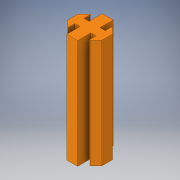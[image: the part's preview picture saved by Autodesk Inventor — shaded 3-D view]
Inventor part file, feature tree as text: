
AUTODESK INVENTOR PART (.ipt)
format: ipt  version: 2019 (Build 230136000, 136)  size: 141,824 bytes
history: native  units: in
note: dims shown in document units (in); Inventor stores cm internally (conversion verified against a paired STEP export)
features: extrude x1, fillet x1, sketch x1
ambient origin geometry x8: Origin, YZ Plane, XZ Plane, XY Plane, X Axis, Y Axis, Z Axis, Center Point
bodies: Body1 (feature_tree)
feature tree (3):
  extrude  "Extrusion2"  Depth=0.655in
  fillet  "Fillet1"  Radius=0.095in
  sketch  "Sketch1"  dims[d0=0.2in d1=0.655in d2=0.095in d4=0.1677in d9=0.121in d12=0.0in d15=0.442in d16=0.442in d20=135.0deg d21=135.0deg d24=0.2437in d25=0.655in d26=0.1372in d33=0.1372in d34=0.121in d35=0.095in d36=0.2437in d37=0.2in d38=0.2in d39=135.0deg d40=135.0deg d41=2.0in d42=0.0in d43=0.01in]
